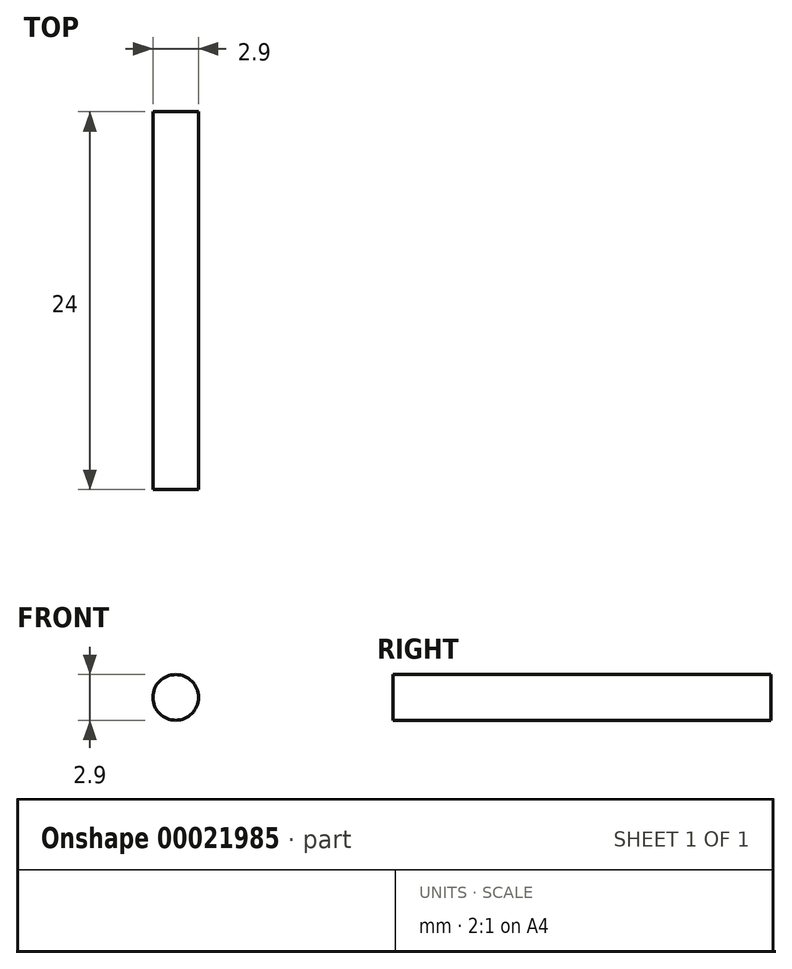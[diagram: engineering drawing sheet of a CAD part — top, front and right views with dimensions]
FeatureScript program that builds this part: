
annotation { "Feature Type Name" : "Feature", "Feature Type Description" : "" }
export const myFeature = defineFeature(function(context is Context, id is Id, definition is map)
    precondition{}
    {
        {
            var Q0;
            Q0=qCreatedBy(makeId("Front.planeOp"),FACE);
            var sketch = newSketch(context, id + "F0", { "sketchPlane" : qUnion([Q0])});
            skCircle(sketch, "E0", {"center": v(0, 0) * mm, "radius": 1.45 * mm});
            skSolve(sketch);
        }
        {
            var Q0;
            Q0 = qSketchRegion(id + "F0", true);
            extrude(context, id + "F1", {"entities" : qUnion([Q0]), "endBound" : BoundingType.SYMMETRIC, "depth" : 24 * mm});
        }
    });
